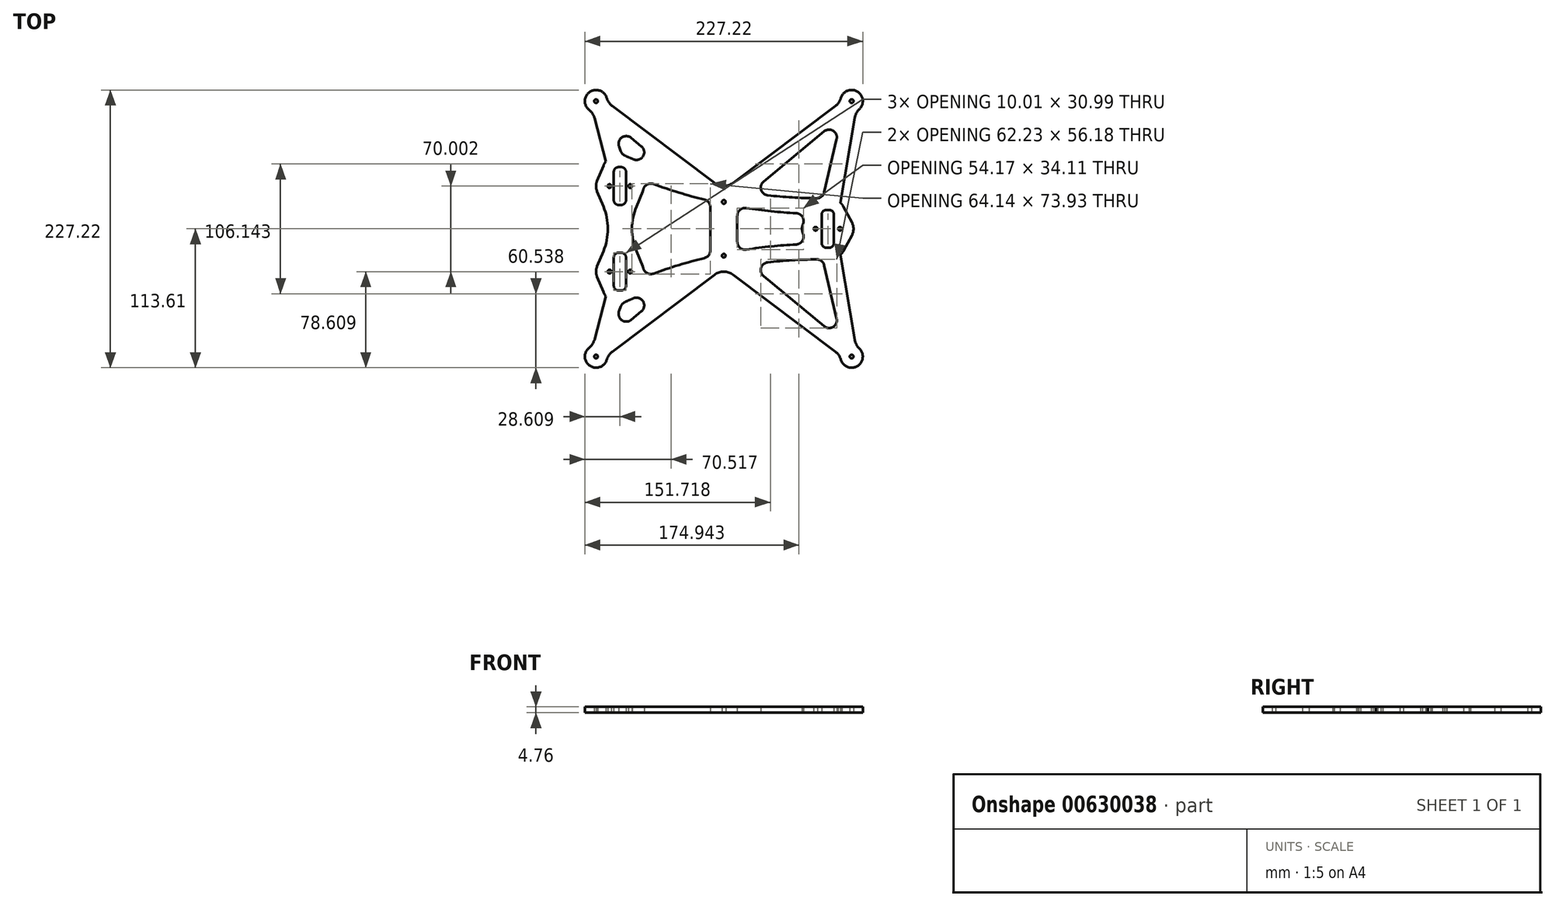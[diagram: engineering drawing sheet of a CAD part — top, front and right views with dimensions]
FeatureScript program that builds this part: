
annotation { "Feature Type Name" : "Feature", "Feature Type Description" : "" }
export const myFeature = defineFeature(function(context is Context, id is Id, definition is map)
    precondition{}
    {
        {
            var Q0;
            Q0=qCreatedBy(makeId("Top.planeOp"),FACE);
            var sketch = newSketch(context, id + "F0", { "sketchPlane" : qUnion([Q0])});
            skLineSegment(sketch, "E0", {"start": v(-14.7, 0) * mm, "end": v(0, 0) * mm, "construction": true});
            skLineSegment(sketch, "E1", {"start": v(0, 0) * mm, "end": v(0, 14.44) * mm, "construction": true});
            skCircle(sketch, "E2", {"center": v(-104.5, 104.5) * mm, "radius": 1.5 * mm});
            skLineSegment(sketch, "E3.bottom", {"start": v(-90, 50.5) * mm, "end": v(-80, 50.5) * mm});
            skLineSegment(sketch, "E3.top", {"start": v(-90, 19.5) * mm, "end": v(-80, 19.5) * mm});
            skLineSegment(sketch, "E3.left", {"start": v(-90, 50.5) * mm, "end": v(-90, 19.5) * mm});
            skLineSegment(sketch, "E3.right", {"start": v(-80, 50.5) * mm, "end": v(-80, 19.5) * mm});
            skLineSegment(sketch, "E4.bottom", {"start": v(80, 15.5) * mm, "end": v(90, 15.5) * mm});
            skLineSegment(sketch, "E4.top", {"start": v(80, -15.5) * mm, "end": v(90, -15.5) * mm});
            skLineSegment(sketch, "E4.left", {"start": v(80, 15.5) * mm, "end": v(80, -15.5) * mm});
            skLineSegment(sketch, "E4.right", {"start": v(90, 15.5) * mm, "end": v(90, -15.5) * mm});
            skCircle(sketch, "E5", {"center": v(-93.5, 35) * mm, "radius": 1.5 * mm});
            skPoint(sketch, "E5.centerSnap0", {"position": v(-90, 35) * mm});
            skCircle(sketch, "E6", {"center": v(-76.5, 35) * mm, "radius": 1.5 * mm});
            skPoint(sketch, "E6.centerSnap0", {"position": v(-80, 35) * mm});
            skCircle(sketch, "E7", {"center": v(0, 22) * mm, "radius": 1.5 * mm});
            skPoint(sketch, "E8", {"position": v(80, 19.5) * mm});
            skLineSegment(sketch, "E9", {"start": v(-85, 50.5) * mm, "end": v(-85, 19.5) * mm, "construction": true});
            skCircle(sketch, "E10.MirrorC", {"center": v(-104.5, -104.5) * mm, "radius": 1.5 * mm});
            skLineSegment(sketch, "E11.MirrorCS", {"start": v(-90, -19.5) * mm, "end": v(-80, -19.5) * mm});
            skLineSegment(sketch, "E12.MirrorCS", {"start": v(-80, -50.5) * mm, "end": v(-80, -19.5) * mm});
            skLineSegment(sketch, "E13.MirrorCS", {"start": v(-90, -50.5) * mm, "end": v(-80, -50.5) * mm});
            skLineSegment(sketch, "E14.MirrorCS", {"start": v(-90, -50.5) * mm, "end": v(-90, -19.5) * mm});
            skCircle(sketch, "E15.MirrorC", {"center": v(104.5, 104.5) * mm, "radius": 1.5 * mm});
            skCircle(sketch, "E16.MirrorC", {"center": v(104.5, -104.5) * mm, "radius": 1.5 * mm});
            skCircle(sketch, "E17.MirrorC", {"center": v(0, -22) * mm, "radius": 1.5 * mm});
            skLineSegment(sketch, "E18", {"start": v(85, 15.5) * mm, "end": v(85, -15.5) * mm, "construction": true});
            skCircle(sketch, "E19.MirrorC", {"center": v(-93.5, -35) * mm, "radius": 1.5 * mm});
            skCircle(sketch, "E20.MirrorC", {"center": v(-76.5, -35) * mm, "radius": 1.5 * mm});
            skCircle(sketch, "E21", {"center": v(75, 0) * mm, "radius": 1.5 * mm});
            skPoint(sketch, "E21.centerSnap0", {"position": v(80, 0) * mm});
            skCircle(sketch, "E22", {"center": v(95, 0) * mm, "radius": 1.5 * mm});
            skPoint(sketch, "E22.centerSnap0", {"position": v(90, 0) * mm});
            skArc(sketch, "E23.0", {"start": v(-104.5, 113.61) * mm, "mid": v(-110.94, 110.94) * mm, "end": v(-113.61, 104.5) * mm});
            skArc(sketch, "E24.MirrorC", {"start": v(-104.5, -113.61) * mm, "mid": v(-110.94, -110.94) * mm, "end": v(-113.61, -104.5) * mm});
            skArc(sketch, "E25.MirrorC", {"start": v(104.5, 113.61) * mm, "mid": v(110.94, 110.94) * mm, "end": v(113.61, 104.5) * mm});
            skArc(sketch, "E26.MirrorC", {"start": v(104.5, -113.61) * mm, "mid": v(110.94, -110.94) * mm, "end": v(113.61, -104.5) * mm});
            skLineSegment(sketch, "E27.bottom", {"start": v(-104.5, 113.61) * mm, "end": v(104.5, 113.61) * mm});
            skLineSegment(sketch, "E27.top", {"start": v(-104.5, -113.61) * mm, "end": v(104.5, -113.61) * mm});
            skLineSegment(sketch, "E27.left", {"start": v(-113.61, 104.5) * mm, "end": v(-113.61, -104.5) * mm});
            skLineSegment(sketch, "E27.right", {"start": v(113.61, 104.5) * mm, "end": v(113.61, -104.5) * mm});
            skSolve(sketch);
        }
        {
            var Q0;
            Q0=makeQuery(id+"F0.imprint","IMPRINT",FACE,{"disambiguationData":[TD([[makeQuery(id+"F0.imprint","IMPRINT",EDGE,{"derivedFrom":sQuery(id+"F0.wireOp",EDGE,"E2")}),-1.0]])]});
            extrude(context, id + "F1", {"entities" : qUnion([Q0]), "depth" : 4.76 * mm, "offsetDistance" : 25.4 * mm});
        }
        {
            var Q0;
            Q0=makeQuery(id+"F1.opExtrude","SWEPT_EDGE",EDGE,{"disambiguationData":[OSD([sQuery(id+"F0.wireOp",EDGE,"E3.bottom"),sQuery(id+"F0.wireOp",EDGE,"E3.right")])]});
            var Q1;
            Q1=makeQuery(id+"F1.opExtrude","SWEPT_EDGE",EDGE,{"disambiguationData":[OSD([sQuery(id+"F0.wireOp",EDGE,"E11.MirrorCS"),sQuery(id+"F0.wireOp",EDGE,"E12.MirrorCS")])]});
            var Q2;
            Q2=makeQuery(id+"F1.opExtrude","SWEPT_EDGE",EDGE,{"disambiguationData":[OSD([sQuery(id+"F0.wireOp",EDGE,"E4.bottom"),sQuery(id+"F0.wireOp",EDGE,"E4.right")])]});
            var Q3;
            Q3=makeQuery(id+"F1.opExtrude","SWEPT_EDGE",EDGE,{"disambiguationData":[OSD([sQuery(id+"F0.wireOp",EDGE,"E4.bottom"),sQuery(id+"F0.wireOp",EDGE,"E4.left")])]});
            var Q4;
            Q4=makeQuery(id+"F1.opExtrude","SWEPT_EDGE",EDGE,{"disambiguationData":[OSD([sQuery(id+"F0.wireOp",EDGE,"E3.bottom"),sQuery(id+"F0.wireOp",EDGE,"E3.left")])]});
            var Q5;
            Q5=makeQuery(id+"F1.opExtrude","SWEPT_EDGE",EDGE,{"disambiguationData":[OSD([sQuery(id+"F0.wireOp",EDGE,"E11.MirrorCS"),sQuery(id+"F0.wireOp",EDGE,"E14.MirrorCS")])]});
            var Q6;
            Q6=makeQuery(id+"F1.opExtrude","SWEPT_EDGE",EDGE,{"disambiguationData":[OSD([sQuery(id+"F0.wireOp",EDGE,"E4.top"),sQuery(id+"F0.wireOp",EDGE,"E4.left")])]});
            var Q7;
            Q7=makeQuery(id+"F1.opExtrude","SWEPT_EDGE",EDGE,{"disambiguationData":[OSD([sQuery(id+"F0.wireOp",EDGE,"E13.MirrorCS"),sQuery(id+"F0.wireOp",EDGE,"E14.MirrorCS")])]});
            var Q8;
            Q8=makeQuery(id+"F1.opExtrude","SWEPT_EDGE",EDGE,{"disambiguationData":[OSD([sQuery(id+"F0.wireOp",EDGE,"E3.top"),sQuery(id+"F0.wireOp",EDGE,"E3.left")])]});
            var Q9;
            Q9=makeQuery(id+"F1.opExtrude","SWEPT_EDGE",EDGE,{"disambiguationData":[OSD([sQuery(id+"F0.wireOp",EDGE,"E12.MirrorCS"),sQuery(id+"F0.wireOp",EDGE,"E13.MirrorCS")])]});
            var Q10;
            Q10=makeQuery(id+"F1.opExtrude","SWEPT_EDGE",EDGE,{"disambiguationData":[OSD([sQuery(id+"F0.wireOp",EDGE,"E3.top"),sQuery(id+"F0.wireOp",EDGE,"E3.right")])]});
            var Q11;
            Q11=makeQuery(id+"F1.opExtrude","SWEPT_EDGE",EDGE,{"disambiguationData":[OSD([sQuery(id+"F0.wireOp",EDGE,"E4.top"),sQuery(id+"F0.wireOp",EDGE,"E4.right")])]});
            fillet(context, id + "F2", {"entities" : qUnion([Q0, Q1, Q2, Q3, Q4, Q5, Q6, Q7, Q8, Q9, Q10, Q11]), "radius" : 4 * mm, "tangentPropagation" : true, "allowEdgeOverflow" : false});
        }
        {
            var Q0;
            Q0=qCreatedBy(makeId("Top.planeOp"),FACE);
            var sketch = newSketch(context, id + "F3", { "sketchPlane" : qUnion([Q0])});
            skArc(sketch, "E28", {"start": v(-66.33, 30.77) * mm, "mid": v(-66.06, 31.49) * mm, "end": v(-65.84, 32.23) * mm});
            skArc(sketch, "E29", {"start": v(-103.68, 39.23) * mm, "mid": v(-104.52, 35) * mm, "end": v(-103.68, 30.77) * mm});
            skLineSegment(sketch, "E30.0", {"start": v(-14.7, 0) * mm, "end": v(0, 0) * mm, "construction": true});
            skLineSegment(sketch, "E30.1", {"start": v(0, 0) * mm, "end": v(0, 14.44) * mm, "construction": true});
            skLineSegment(sketch, "E31.0", {"start": v(-86.02, 60.02) * mm, "end": v(-83.99, 60.02) * mm});
            skArc(sketch, "E31.1", {"start": v(-98.5, 51.7) * mm, "mid": v(-97.6, 53.45) * mm, "end": v(-96.48, 55.06) * mm});
            skArc(sketch, "E31.2", {"start": v(-83.99, 60.02) * mm, "mid": v(-81.15, 59.72) * mm, "end": v(-78.44, 58.83) * mm, "construction": true});
            skArc(sketch, "E31.5", {"start": v(-71.5, 18.3) * mm, "mid": v(-76.49, 12.25) * mm, "end": v(-83.99, 9.98) * mm, "construction": true});
            skLineSegment(sketch, "E31.6", {"start": v(-86.02, 9.98) * mm, "end": v(-83.99, 9.98) * mm, "construction": true});
            skArc(sketch, "E31.7", {"start": v(-86.02, 9.98) * mm, "mid": v(-93.52, 12.25) * mm, "end": v(-98.5, 18.3) * mm, "construction": true});
            skLineSegment(sketch, "E32", {"start": v(-98.5, 51.7) * mm, "end": v(-103.68, 39.23) * mm});
            skLineSegment(sketch, "E33", {"start": v(-103.68, 30.77) * mm, "end": v(-98.5, 18.3) * mm});
            skLineSegment(sketch, "E34", {"start": v(-71.5, 18.3) * mm, "end": v(-66.33, 30.77) * mm});
            skLineSegment(sketch, "E35", {"start": v(-66.33, 39.23) * mm, "end": v(-71.5, 51.7) * mm});
            skLineSegment(sketch, "E36.MirrorCS", {"start": v(-86.02, -60.02) * mm, "end": v(-83.99, -60.02) * mm});
            skLineSegment(sketch, "E37.MirrorCS", {"start": v(-86.02, -9.98) * mm, "end": v(-83.99, -9.98) * mm, "construction": true});
            skArc(sketch, "E38.MirrorCS", {"start": v(-66.33, -30.77) * mm, "mid": v(-66.06, -31.49) * mm, "end": v(-65.84, -32.23) * mm});
            skLineSegment(sketch, "E39.MirrorCS", {"start": v(-103.68, -30.77) * mm, "end": v(-98.5, -18.3) * mm});
            skLineSegment(sketch, "E40.MirrorCS", {"start": v(-71.5, -18.3) * mm, "end": v(-66.33, -30.77) * mm});
            skArc(sketch, "E41.MirrorCS", {"start": v(-86.02, -9.98) * mm, "mid": v(-93.52, -12.25) * mm, "end": v(-98.5, -18.3) * mm, "construction": true});
            skArc(sketch, "E42.MirrorCS", {"start": v(-71.5, -18.3) * mm, "mid": v(-76.49, -12.25) * mm, "end": v(-83.99, -9.98) * mm, "construction": true});
            skLineSegment(sketch, "E43.MirrorCS", {"start": v(-66.33, -39.23) * mm, "end": v(-71.5, -51.7) * mm});
            skLineSegment(sketch, "E44.MirrorCS", {"start": v(-98.5, -51.7) * mm, "end": v(-103.68, -39.23) * mm});
            skArc(sketch, "E45.MirrorCS", {"start": v(-83.99, -60.02) * mm, "mid": v(-76.49, -57.75) * mm, "end": v(-71.5, -51.7) * mm});
            skArc(sketch, "E46.MirrorCS", {"start": v(-103.68, -39.23) * mm, "mid": v(-104.52, -35) * mm, "end": v(-103.68, -30.77) * mm});
            skArc(sketch, "E47.MirrorCS", {"start": v(-98.5, -51.7) * mm, "mid": v(-97.6, -53.45) * mm, "end": v(-96.48, -55.06) * mm});
            skArc(sketch, "E48", {"start": v(11.02, 22) * mm, "mid": v(0, 33.02) * mm, "end": v(-11.02, 22) * mm});
            skArc(sketch, "E49", {"start": v(-11.02, -22) * mm, "mid": v(0, -33.02) * mm, "end": v(11.02, -22) * mm});
            skLineSegment(sketch, "E50", {"start": v(-11.02, 17.7) * mm, "end": v(-11.02, -17.7) * mm});
            skLineSegment(sketch, "E51", {"start": v(11.02, 22) * mm, "end": v(11.02, 18.2) * mm});
            skArc(sketch, "E52.1", {"start": v(76.61, -22.83) * mm, "mid": v(74.03, -20.64) * mm, "end": v(72.07, -17.88) * mm});
            skArc(sketch, "E52.2", {"start": v(72.07, 17.88) * mm, "mid": v(73.56, 20.1) * mm, "end": v(75.45, 21.98) * mm});
            skArc(sketch, "E52.5", {"start": v(95.35, 21.28) * mm, "mid": v(96.78, 19.68) * mm, "end": v(97.93, 17.88) * mm});
            skArc(sketch, "E53", {"start": v(64.77, 4.09) * mm, "mid": v(64, -0.61) * mm, "end": v(65.29, -5.2) * mm});
            skArc(sketch, "E54", {"start": v(104.72, -5.2) * mm, "mid": v(106.02, 0) * mm, "end": v(104.72, 5.2) * mm});
            skLineSegment(sketch, "E55", {"start": v(72.07, 17.88) * mm, "end": v(65.29, 5.2) * mm});
            skLineSegment(sketch, "E56", {"start": v(65.29, -5.2) * mm, "end": v(72.07, -17.88) * mm});
            skLineSegment(sketch, "E57", {"start": v(97.93, -17.88) * mm, "end": v(104.72, -5.2) * mm});
            skLineSegment(sketch, "E58", {"start": v(104.72, 5.2) * mm, "end": v(97.93, 17.88) * mm});
            skArc(sketch, "E59", {"start": v(-83.39, 61.1) * mm, "mid": v(-61.1, 51.54) * mm, "end": v(-38.26, 43.4) * mm});
            skArc(sketch, "E60.MirrorCS", {"start": v(-83.39, -61.1) * mm, "mid": v(-61.1, -51.54) * mm, "end": v(-38.26, -43.4) * mm});
            skArc(sketch, "E61.MirrorCS", {"start": v(95.35, -21.28) * mm, "mid": v(96.78, -19.68) * mm, "end": v(97.93, -17.88) * mm});
            skLineSegment(sketch, "E62.MirrorCS", {"start": v(97.93, 17.88) * mm, "end": v(104.72, 5.2) * mm});
            skPoint(sketch, "E63.orphan", {"position": v(80.94, 49.64) * mm});
            skPoint(sketch, "E64.orphan", {"position": v(80.94, -49.64) * mm});
            skArc(sketch, "E65", {"start": v(-98.5, -18.3) * mm, "mid": v(-94.84, 0) * mm, "end": v(-98.5, 18.3) * mm});
            skArc(sketch, "E66", {"start": v(-71.5, 18.3) * mm, "mid": v(-75.16, 0) * mm, "end": v(-71.5, -18.3) * mm});
            skArc(sketch, "E67.0", {"start": v(-57.5, 36.6) * mm, "mid": v(-36.85, 29.65) * mm, "end": v(-15.85, 23.86) * mm});
            skArc(sketch, "E68", {"start": v(-57.5, 36.6) * mm, "mid": v(-62.64, 36.26) * mm, "end": v(-65.84, 32.23) * mm});
            skArc(sketch, "E69", {"start": v(-11.02, 17.7) * mm, "mid": v(-12.37, 21.6) * mm, "end": v(-15.85, 23.86) * mm});
            skArc(sketch, "E70", {"start": v(18.35, 16.99) * mm, "mid": v(13.24, 15.54) * mm, "end": v(11.02, 10.72) * mm});
            skArc(sketch, "E71", {"start": v(64.77, 4.09) * mm, "mid": v(64.22, 9.87) * mm, "end": v(59.2, 12.78) * mm});
            skArc(sketch, "E72.trimOffspring", {"start": v(18.35, 16.99) * mm, "mid": v(38.72, 14.36) * mm, "end": v(59.2, 12.78) * mm});
            skLineSegment(sketch, "E73.trimOffspring", {"start": v(11.02, 10.72) * mm, "end": v(11.02, -10.72) * mm});
            skArc(sketch, "E74.MirrorCS", {"start": v(64.77, -4.09) * mm, "mid": v(64.22, -9.87) * mm, "end": v(59.2, -12.78) * mm});
            skArc(sketch, "E75.MirrorCS", {"start": v(18.35, -16.99) * mm, "mid": v(38.72, -14.36) * mm, "end": v(59.2, -12.78) * mm});
            skArc(sketch, "E76.MirrorCS", {"start": v(18.35, -16.99) * mm, "mid": v(13.24, -15.54) * mm, "end": v(11.02, -10.72) * mm});
            skArc(sketch, "E77.MirrorCS", {"start": v(-11.02, -17.7) * mm, "mid": v(-12.37, -21.6) * mm, "end": v(-15.85, -23.86) * mm});
            skArc(sketch, "E78.MirrorCS", {"start": v(-57.5, -36.6) * mm, "mid": v(-36.85, -29.65) * mm, "end": v(-15.85, -23.86) * mm});
            skArc(sketch, "E79.MirrorCS", {"start": v(-57.5, -36.6) * mm, "mid": v(-62.64, -36.26) * mm, "end": v(-65.84, -32.23) * mm});
            skPoint(sketch, "E80.centerSnap0", {"position": v(-85, 60.02) * mm});
            skCircle(sketch, "E81", {"center": v(-104.5, 104.5) * mm, "radius": 4.76 * mm, "construction": true});
            skCircle(sketch, "E82", {"center": v(104.5, 104.5) * mm, "radius": 4.76 * mm, "construction": true});
            skCircle(sketch, "E83", {"center": v(85, 7.56) * mm, "radius": 7.94 * mm, "construction": true});
            skCircle(sketch, "E84", {"center": v(0, 22) * mm, "radius": 7.94 * mm, "construction": true});
            skPoint(sketch, "E84.centerSnap0", {"position": v(0, 7.22) * mm});
            skCircle(sketch, "E85", {"center": v(-85, 42.56) * mm, "radius": 7.94 * mm, "construction": true});
            skPoint(sketch, "E86", {"position": v(-85, 50.5) * mm});
            skPoint(sketch, "E87", {"position": v(85, 15.5) * mm});
            skArc(sketch, "E88", {"start": v(-95.42, 103.63) * mm, "mid": v(-109.58, 112.07) * mm, "end": v(-107.13, 95.77) * mm});
            skArc(sketch, "E89", {"start": v(107.9, 96.04) * mm, "mid": v(109.23, 112.29) * mm, "end": v(95.42, 103.63) * mm});
            skLineSegment(sketch, "E90", {"start": v(95.42, 103.63) * mm, "end": v(7.63, 37.66) * mm});
            skLineSegment(sketch, "E91", {"start": v(21.34, 29.38) * mm, "end": v(96.62, 91.78) * mm});
            skLineSegment(sketch, "E92", {"start": v(107.9, 96.04) * mm, "end": v(95.35, 21.28) * mm});
            skLineSegment(sketch, "E93", {"start": v(80.94, 24.97) * mm, "end": v(96.62, 91.78) * mm});
            skPoint(sketch, "E94.orphan", {"position": v(104.72, 126.27) * mm});
            skPoint(sketch, "E95.orphan", {"position": v(85.8, 25.02) * mm});
            skArc(sketch, "E96.trimOffspring", {"start": v(21.34, 29.38) * mm, "mid": v(51.05, 26.02) * mm, "end": v(80.94, 24.97) * mm});
            skLineSegment(sketch, "E97", {"start": v(-107.13, 95.77) * mm, "end": v(-96.48, 55.06) * mm});
            skLineSegment(sketch, "E98", {"start": v(-83.39, 61.1) * mm, "end": v(-93.88, 89.51) * mm});
            skLineSegment(sketch, "E99", {"start": v(-95.42, 103.63) * mm, "end": v(-7.63, 37.66) * mm});
            skLineSegment(sketch, "E100", {"start": v(-38.26, 43.4) * mm, "end": v(-93.88, 89.51) * mm});
            skArc(sketch, "E101.trimOffspring", {"start": v(-2.48, 33.79) * mm, "mid": v(-0.55, 33.37) * mm, "end": v(1.38, 32.97) * mm});
            skPoint(sketch, "E102.orphan", {"position": v(-104.5, 98.3) * mm});
            skCircle(sketch, "E103.MirrorC", {"center": v(104.5, -104.5) * mm, "radius": 4.76 * mm, "construction": true});
            skLineSegment(sketch, "E104.MirrorCS", {"start": v(80.94, -24.97) * mm, "end": v(96.62, -91.78) * mm});
            skPoint(sketch, "E105.MirrorP", {"position": v(104.72, -126.27) * mm});
            skLineSegment(sketch, "E106.MirrorCS", {"start": v(21.34, -29.38) * mm, "end": v(96.62, -91.78) * mm});
            skLineSegment(sketch, "E107.MirrorCS", {"start": v(95.42, -103.63) * mm, "end": v(7.63, -37.66) * mm});
            skLineSegment(sketch, "E108.MirrorCS", {"start": v(107.9, -96.04) * mm, "end": v(95.35, -21.28) * mm});
            skArc(sketch, "E109.MirrorCS", {"start": v(107.9, -96.04) * mm, "mid": v(109.23, -112.29) * mm, "end": v(95.42, -103.63) * mm});
            skLineSegment(sketch, "E110.MirrorCS", {"start": v(-38.26, -43.4) * mm, "end": v(-93.88, -89.51) * mm});
            skCircle(sketch, "E111.MirrorC", {"center": v(-104.5, -104.5) * mm, "radius": 4.76 * mm, "construction": true});
            skLineSegment(sketch, "E112.MirrorCS", {"start": v(-83.39, -61.1) * mm, "end": v(-93.88, -89.51) * mm});
            skArc(sketch, "E113.MirrorCS", {"start": v(-95.42, -103.63) * mm, "mid": v(-109.58, -112.07) * mm, "end": v(-107.13, -95.77) * mm});
            skLineSegment(sketch, "E114.MirrorCS", {"start": v(-107.13, -95.77) * mm, "end": v(-96.48, -55.06) * mm});
            skLineSegment(sketch, "E115.MirrorCS", {"start": v(-95.42, -103.63) * mm, "end": v(-7.63, -37.66) * mm});
            skPoint(sketch, "E116.MirrorP", {"position": v(-104.5, -98.3) * mm});
            skPoint(sketch, "E117.orphan", {"position": v(85.8, -25.02) * mm});
            skArc(sketch, "E118.trimOffspring", {"start": v(21.34, -29.38) * mm, "mid": v(51.05, -26.02) * mm, "end": v(80.94, -24.97) * mm});
            skArc(sketch, "E119.trimOffspring", {"start": v(-2.48, -33.79) * mm, "mid": v(-0.13, -33.28) * mm, "end": v(2.21, -32.8) * mm});
            skPoint(sketch, "E120.orphan", {"position": v(-78.44, -58.83) * mm});
            skArc(sketch, "E121", {"start": v(-7.63, 37.66) * mm, "mid": v(0, 35.11) * mm, "end": v(7.63, 37.66) * mm});
            skArc(sketch, "E122.MirrorCS", {"start": v(-7.63, -37.66) * mm, "mid": v(0, -35.11) * mm, "end": v(7.63, -37.66) * mm});
            skPoint(sketch, "E123.orphan", {"position": v(1.38, -32.97) * mm});
            skSolve(sketch);
        }
        {
            var Q0;
            Q0 = qSketchRegion(id + "F3", true);
            extrude(context, id + "F4", {"entities" : qUnion([Q0]), "depth" : 25.4 * mm, "offsetDistance" : 25.4 * mm});
        }
        {
            var Q0;
            Q0=makeQuery(id+"F4.opExtrude","SWEPT_EDGE",EDGE,{"disambiguationData":[OSD([sQuery(id+"F3.wireOp",EDGE,"E104.MirrorCS"),sQuery(id+"F3.wireOp",EDGE,"E118.trimOffspring")])]});
            var Q1;
            Q1=makeQuery(id+"F4.opExtrude","SWEPT_EDGE",EDGE,{"disambiguationData":[OSD([sQuery(id+"F3.wireOp",EDGE,"E91"),sQuery(id+"F3.wireOp",EDGE,"E93")])]});
            var Q2;
            Q2=makeQuery(id+"F4.opExtrude","SWEPT_EDGE",EDGE,{"disambiguationData":[OSD([sQuery(id+"F3.wireOp",EDGE,"E98"),sQuery(id+"F3.wireOp",EDGE,"E100")])]});
            var Q3;
            Q3=makeQuery(id+"F4.opExtrude","SWEPT_EDGE",EDGE,{"disambiguationData":[OSD([sQuery(id+"F3.wireOp",EDGE,"E60.MirrorCS"),sQuery(id+"F3.wireOp",EDGE,"E112.MirrorCS")])]});
            var Q4;
            Q4=makeQuery(id+"F4.opExtrude","SWEPT_EDGE",EDGE,{"disambiguationData":[OSD([sQuery(id+"F3.wireOp",EDGE,"E106.MirrorCS"),sQuery(id+"F3.wireOp",EDGE,"E118.trimOffspring")])]});
            var Q5;
            Q5=makeQuery(id+"F4.opExtrude","SWEPT_EDGE",EDGE,{"disambiguationData":[OSD([sQuery(id+"F3.wireOp",EDGE,"E104.MirrorCS"),sQuery(id+"F3.wireOp",EDGE,"E106.MirrorCS")])]});
            var Q6;
            Q6=makeQuery(id+"F4.opExtrude","SWEPT_EDGE",EDGE,{"disambiguationData":[OSD([sQuery(id+"F3.wireOp",EDGE,"E110.MirrorCS"),sQuery(id+"F3.wireOp",EDGE,"E112.MirrorCS")])]});
            var Q7;
            Q7=makeQuery(id+"F4.opExtrude","SWEPT_EDGE",EDGE,{"disambiguationData":[OSD([sQuery(id+"F3.wireOp",EDGE,"E60.MirrorCS"),sQuery(id+"F3.wireOp",EDGE,"E110.MirrorCS")])]});
            var Q8;
            Q8=makeQuery(id+"F4.opExtrude","SWEPT_EDGE",EDGE,{"disambiguationData":[OSD([sQuery(id+"F3.wireOp",EDGE,"E93"),sQuery(id+"F3.wireOp",EDGE,"E96.trimOffspring")])]});
            var Q9;
            Q9=makeQuery(id+"F4.opExtrude","SWEPT_EDGE",EDGE,{"disambiguationData":[OSD([sQuery(id+"F3.wireOp",EDGE,"E59"),sQuery(id+"F3.wireOp",EDGE,"E100")])]});
            var Q10;
            Q10=makeQuery(id+"F4.opExtrude","SWEPT_EDGE",EDGE,{"disambiguationData":[OSD([sQuery(id+"F3.wireOp",EDGE,"E59"),sQuery(id+"F3.wireOp",EDGE,"E98")])]});
            var Q11;
            Q11=makeQuery(id+"F4.opExtrude","SWEPT_EDGE",EDGE,{"disambiguationData":[OSD([sQuery(id+"F3.wireOp",EDGE,"E91"),sQuery(id+"F3.wireOp",EDGE,"E96.trimOffspring")])]});
            fillet(context, id + "F5", {"entities" : qUnion([Q0, Q1, Q2, Q3, Q4, Q5, Q6, Q7, Q8, Q9, Q10, Q11]), "radius" : 6.35 * mm, "tangentPropagation" : true, "allowEdgeOverflow" : false});
        }
        {
            var Q0;
            Q0=makeQuery(id+"F4.opExtrude","SWEPT_EDGE",EDGE,{"disambiguationData":[OSD([sQuery(id+"F3.wireOp",EDGE,"E88"),sQuery(id+"F3.wireOp",EDGE,"E99")])]});
            var Q1;
            Q1=makeQuery(id+"F4.opExtrude","SWEPT_EDGE",EDGE,{"disambiguationData":[OSD([sQuery(id+"F3.wireOp",EDGE,"E89"),sQuery(id+"F3.wireOp",EDGE,"E90")])]});
            var Q2;
            Q2=makeQuery(id+"F4.opExtrude","SWEPT_EDGE",EDGE,{"disambiguationData":[OSD([sQuery(id+"F3.wireOp",EDGE,"E113.MirrorCS"),sQuery(id+"F3.wireOp",EDGE,"E114.MirrorCS")])]});
            var Q3;
            Q3=makeQuery(id+"F4.opExtrude","SWEPT_EDGE",EDGE,{"disambiguationData":[OSD([sQuery(id+"F3.wireOp",EDGE,"E88"),sQuery(id+"F3.wireOp",EDGE,"E97")])]});
            var Q4;
            Q4=makeQuery(id+"F4.opExtrude","SWEPT_EDGE",EDGE,{"disambiguationData":[OSD([sQuery(id+"F3.wireOp",EDGE,"E107.MirrorCS"),sQuery(id+"F3.wireOp",EDGE,"E109.MirrorCS")])]});
            var Q5;
            Q5=makeQuery(id+"F4.opExtrude","SWEPT_EDGE",EDGE,{"disambiguationData":[OSD([sQuery(id+"F3.wireOp",EDGE,"E113.MirrorCS"),sQuery(id+"F3.wireOp",EDGE,"E115.MirrorCS")])]});
            var Q6;
            Q6=makeQuery(id+"F4.opExtrude","SWEPT_EDGE",EDGE,{"disambiguationData":[OSD([sQuery(id+"F3.wireOp",EDGE,"E108.MirrorCS"),sQuery(id+"F3.wireOp",EDGE,"E109.MirrorCS")])]});
            var Q7;
            Q7=makeQuery(id+"F4.opExtrude","SWEPT_EDGE",EDGE,{"disambiguationData":[OSD([sQuery(id+"F3.wireOp",EDGE,"E89"),sQuery(id+"F3.wireOp",EDGE,"E92")])]});
            fillet(context, id + "F6", {"entities" : qUnion([Q0, Q1, Q2, Q3, Q4, Q5, Q6, Q7]), "radius" : 12.7 * mm, "tangentPropagation" : true, "allowEdgeOverflow" : false});
        }
        {
            var Q0;
            Q0=makeQuery(id+"F4.opExtrude","SWEPT_BODY",BODY,{"disambiguationData":[OSD([sQuery(id+"F3.wireOp",EDGE,"E28"),sQuery(id+"F3.wireOp",EDGE,"E29"),sQuery(id+"F3.wireOp",EDGE,"E31.1"),sQuery(id+"F3.wireOp",EDGE,"E32"),sQuery(id+"F3.wireOp",EDGE,"E33"),sQuery(id+"F3.wireOp",EDGE,"E34"),sQuery(id+"F3.wireOp",EDGE,"E38.MirrorCS"),sQuery(id+"F3.wireOp",EDGE,"E39.MirrorCS"),sQuery(id+"F3.wireOp",EDGE,"E40.MirrorCS"),sQuery(id+"F3.wireOp",EDGE,"E44.MirrorCS"),sQuery(id+"F3.wireOp",EDGE,"E46.MirrorCS"),sQuery(id+"F3.wireOp",EDGE,"E47.MirrorCS"),sQuery(id+"F3.wireOp",EDGE,"E50"),sQuery(id+"F3.wireOp",EDGE,"E53"),sQuery(id+"F3.wireOp",EDGE,"E54"),sQuery(id+"F3.wireOp",EDGE,"E57"),sQuery(id+"F3.wireOp",EDGE,"E59"),sQuery(id+"F3.wireOp",EDGE,"E60.MirrorCS"),sQuery(id+"F3.wireOp",EDGE,"E61.MirrorCS"),sQuery(id+"F3.wireOp",EDGE,"E62.MirrorCS"),sQuery(id+"F3.wireOp",EDGE,"E52.5"),sQuery(id+"F3.wireOp",EDGE,"E65"),sQuery(id+"F3.wireOp",EDGE,"E66"),sQuery(id+"F3.wireOp",EDGE,"E67.0"),sQuery(id+"F3.wireOp",EDGE,"E68"),sQuery(id+"F3.wireOp",EDGE,"E69"),sQuery(id+"F3.wireOp",EDGE,"E70"),sQuery(id+"F3.wireOp",EDGE,"E71"),sQuery(id+"F3.wireOp",EDGE,"E72.trimOffspring"),sQuery(id+"F3.wireOp",EDGE,"E73.trimOffspring"),sQuery(id+"F3.wireOp",EDGE,"E74.MirrorCS"),sQuery(id+"F3.wireOp",EDGE,"E75.MirrorCS"),sQuery(id+"F3.wireOp",EDGE,"E76.MirrorCS"),sQuery(id+"F3.wireOp",EDGE,"E77.MirrorCS"),sQuery(id+"F3.wireOp",EDGE,"E78.MirrorCS"),sQuery(id+"F3.wireOp",EDGE,"E79.MirrorCS"),sQuery(id+"F3.wireOp",EDGE,"E88"),sQuery(id+"F3.wireOp",EDGE,"E89"),sQuery(id+"F3.wireOp",EDGE,"E90"),sQuery(id+"F3.wireOp",EDGE,"E91"),sQuery(id+"F3.wireOp",EDGE,"E92"),sQuery(id+"F3.wireOp",EDGE,"E93"),sQuery(id+"F3.wireOp",EDGE,"E96.trimOffspring"),sQuery(id+"F3.wireOp",EDGE,"E97"),sQuery(id+"F3.wireOp",EDGE,"E98"),sQuery(id+"F3.wireOp",EDGE,"E99"),sQuery(id+"F3.wireOp",EDGE,"E100"),sQuery(id+"F3.wireOp",EDGE,"E104.MirrorCS"),sQuery(id+"F3.wireOp",EDGE,"E106.MirrorCS"),sQuery(id+"F3.wireOp",EDGE,"E107.MirrorCS"),sQuery(id+"F3.wireOp",EDGE,"E108.MirrorCS"),sQuery(id+"F3.wireOp",EDGE,"E109.MirrorCS"),sQuery(id+"F3.wireOp",EDGE,"E110.MirrorCS"),sQuery(id+"F3.wireOp",EDGE,"E112.MirrorCS"),sQuery(id+"F3.wireOp",EDGE,"E113.MirrorCS"),sQuery(id+"F3.wireOp",EDGE,"E114.MirrorCS"),sQuery(id+"F3.wireOp",EDGE,"E115.MirrorCS"),sQuery(id+"F3.wireOp",EDGE,"E118.trimOffspring"),sQuery(id+"F3.wireOp",EDGE,"E121"),sQuery(id+"F3.wireOp",EDGE,"E122.MirrorCS")])]});
            var Q1;
            Q1=makeQuery(id+"F1.opExtrude","SWEPT_BODY",BODY,{"disambiguationData":[OSD([sQuery(id+"F0.wireOp",EDGE,"E2"),sQuery(id+"F0.wireOp",EDGE,"E3.bottom"),sQuery(id+"F0.wireOp",EDGE,"E3.top"),sQuery(id+"F0.wireOp",EDGE,"E3.left"),sQuery(id+"F0.wireOp",EDGE,"E3.right"),sQuery(id+"F0.wireOp",EDGE,"E4.bottom"),sQuery(id+"F0.wireOp",EDGE,"E4.top"),sQuery(id+"F0.wireOp",EDGE,"E4.left"),sQuery(id+"F0.wireOp",EDGE,"E4.right"),sQuery(id+"F0.wireOp",EDGE,"E5"),sQuery(id+"F0.wireOp",EDGE,"E6"),sQuery(id+"F0.wireOp",EDGE,"E7"),sQuery(id+"F0.wireOp",EDGE,"E10.MirrorC"),sQuery(id+"F0.wireOp",EDGE,"E11.MirrorCS"),sQuery(id+"F0.wireOp",EDGE,"E12.MirrorCS"),sQuery(id+"F0.wireOp",EDGE,"E13.MirrorCS"),sQuery(id+"F0.wireOp",EDGE,"E14.MirrorCS"),sQuery(id+"F0.wireOp",EDGE,"E15.MirrorC"),sQuery(id+"F0.wireOp",EDGE,"E16.MirrorC"),sQuery(id+"F0.wireOp",EDGE,"E17.MirrorC"),sQuery(id+"F0.wireOp",EDGE,"E19.MirrorC"),sQuery(id+"F0.wireOp",EDGE,"E20.MirrorC"),sQuery(id+"F0.wireOp",EDGE,"E21"),sQuery(id+"F0.wireOp",EDGE,"E22"),sQuery(id+"F0.wireOp",EDGE,"E23.0"),sQuery(id+"F0.wireOp",EDGE,"E24.MirrorC"),sQuery(id+"F0.wireOp",EDGE,"E25.MirrorC"),sQuery(id+"F0.wireOp",EDGE,"E26.MirrorC"),sQuery(id+"F0.wireOp",EDGE,"E27.bottom"),sQuery(id+"F0.wireOp",EDGE,"E27.top"),sQuery(id+"F0.wireOp",EDGE,"E27.left"),sQuery(id+"F0.wireOp",EDGE,"E27.right")])]});
            booleanBodies(context, id + "F7", {"operationType" : BooleanOperationType.INTERSECTION, "tools" : qUnion([Q0, Q1])});
        }
    });
